# Revit family: Simone Double Sconce
name_source: partatom
category: Lighting Fixtures
revit_build: Autodesk Revit 2017 (Build: 20190508_0315(x64)
units: mm (PartAtom-declared; Revit-internal decimal feet)

## family parameters
Cut with Voids When Loaded = No
Host = Face
Light Source = Yes
Part Type = Normal
Room Calculation Point = No
Round Connector Dimension = Use Diameter
Shared = No

## types (1)
- Simone Double Sconce
    Canopy Width = 5"
    Color Filter = 16777215
    Cost = 379 $
    Default Elevation = 0"
    Description = An elegant expression of scale and balance, the Simone Collection is inspired by the early-1960’s Jazz era. Luxurious and versatile with a playful edge, this beautifully crafted family of solid brass functional sculpture creates a cascading pattern of graphic line and glowing light, bringing an eye-catching visual element to any space. Assembled in our Portland, Ore. factory using ethically-sourced domestic and global components. A Schoolhouse Original.
    Dimming Lamp Color Temperature Shift = <None>
    Height = 17"
    Light Source Symbol Size = 5"
    Max Wattage = 60 W
    Primary Finishes = Natural Brass, True Black
    Product Material = Schoolhouse_Brass
    URL = https://www.schoolhouse.com
    Voltage = 120/220 V
    Width = 10"

## geometry (parser evidence)
native form markers: Sweep x3
no freeform markers — native parametric forms only
